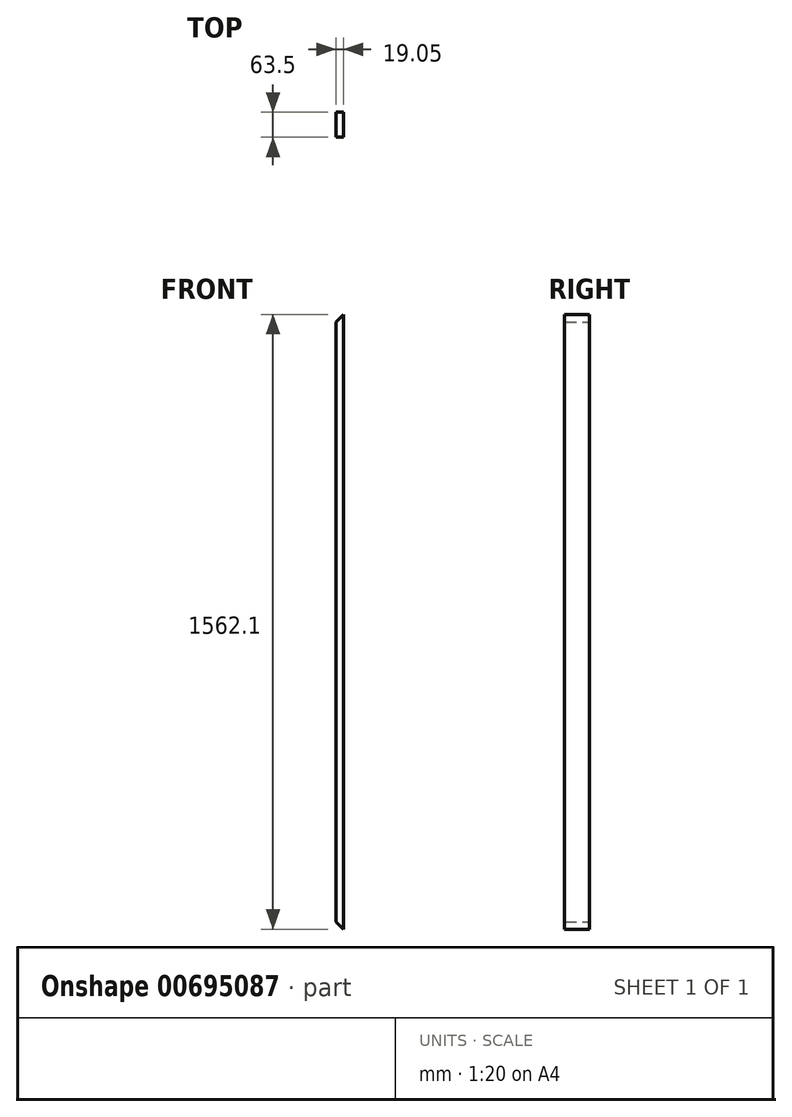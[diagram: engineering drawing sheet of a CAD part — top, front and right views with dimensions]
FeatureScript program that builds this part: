
annotation { "Feature Type Name" : "Feature", "Feature Type Description" : "" }
export const myFeature = defineFeature(function(context is Context, id is Id, definition is map)
    precondition{}
    {
        {
            var Q0;
            Q0=qCreatedBy(makeId("Top.planeOp"),FACE);
            var sketch = newSketch(context, id + "F0", { "sketchPlane" : qUnion([Q0])});
            skLineSegment(sketch, "E0.bottom", {"start": v(0, 0) * mm, "end": v(19.05, 0) * mm});
            skLineSegment(sketch, "E0.top", {"start": v(0, 63.5) * mm, "end": v(19.05, 63.5) * mm});
            skLineSegment(sketch, "E0.left", {"start": v(0, 0) * mm, "end": v(0, 63.5) * mm});
            skLineSegment(sketch, "E0.right", {"start": v(19.05, 0) * mm, "end": v(19.05, 63.5) * mm});
            skSolve(sketch);
        }
        {
            var Q0;
            Q0=makeQuery(id+"F0.imprint","IMPRINT",FACE,{"disambiguationData":[TD([[makeQuery(id+"F0.imprint","IMPRINT",EDGE,{"derivedFrom":sQuery(id+"F0.wireOp",EDGE,"E0.bottom")}),1.0]])]});
            extrude(context, id + "F1", {"entities" : qUnion([Q0]), "depth" : 1562.1 * mm, "offsetDistance" : 25.4 * mm});
        }
        {
            var Q0;
            Q0=makeQuery(id+"F1.opExtrude","SWEPT_FACE",FACE,{"disambiguationData":[OSD([sQuery(id+"F0.wireOp",EDGE,"E0.top")])]});
            var sketch = newSketch(context, id + "F2", { "sketchPlane" : qUnion([Q0])});
            skLineSegment(sketch, "E1", {"start": v(-19.05, 0) * mm, "end": v(0, 19.05) * mm});
            skLineSegment(sketch, "E2", {"start": v(-19.05, 0) * mm, "end": v(0, 0) * mm});
            skLineSegment(sketch, "E3", {"start": v(0, 0) * mm, "end": v(0, 19.05) * mm});
            skSolve(sketch);
        }
        {
            var Q0;
            Q0=makeQuery(id+"F2.imprint","IMPRINT",FACE,{"disambiguationData":[TD([[makeQuery(id+"F2.imprint","IMPRINT",EDGE,{"derivedFrom":sQuery(id+"F2.wireOp",EDGE,"E1")}),-1.0]])]});
            extrude(context, id + "F3", {"entities" : qUnion([Q0]), "operationType" : NewBodyOperationType.REMOVE, "endBound" : BoundingType.THROUGH_ALL, "oppositeDirection" : true, "depth" : 25.4 * mm, "offsetDistance" : 25.4 * mm});
        }
        {
            var Q0;
            Q0=makeQuery(id+"F1.opExtrude","SWEPT_FACE",FACE,{"disambiguationData":[OSD([sQuery(id+"F0.wireOp",EDGE,"E0.top")])]});
            var sketch = newSketch(context, id + "F4", { "sketchPlane" : qUnion([Q0])});
            skLineSegment(sketch, "E4", {"start": v(-19.05, 1562.1) * mm, "end": v(0, 1562.1) * mm});
            skLineSegment(sketch, "E5", {"start": v(0, 1562.1) * mm, "end": v(0, 1543.05) * mm});
            skLineSegment(sketch, "E6", {"start": v(0, 1543.05) * mm, "end": v(-19.05, 1562.1) * mm});
            skSolve(sketch);
        }
        {
            var Q0;
            Q0 = qSketchRegion(id + "F4", true);
            extrude(context, id + "F5", {"entities" : qUnion([Q0]), "operationType" : NewBodyOperationType.REMOVE, "endBound" : BoundingType.THROUGH_ALL, "oppositeDirection" : true, "depth" : 25.4 * mm, "offsetDistance" : 25.4 * mm});
        }
    });
